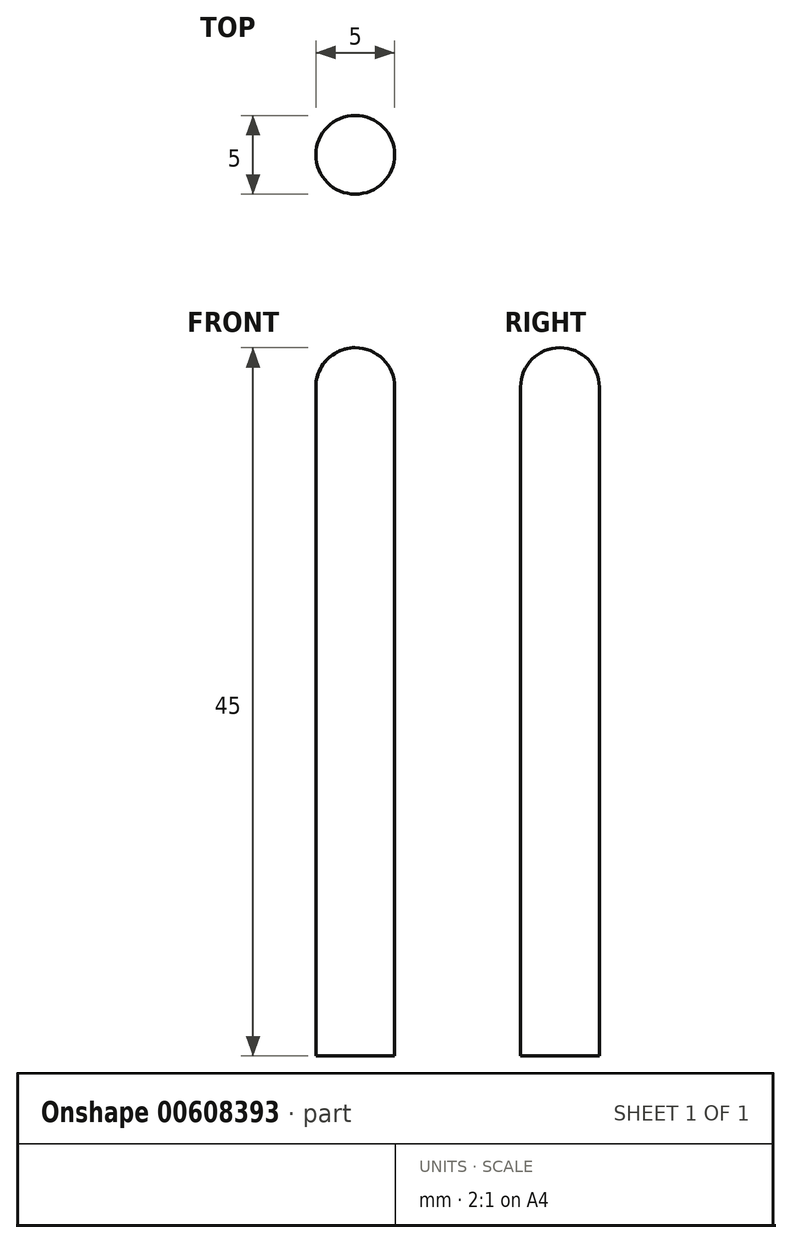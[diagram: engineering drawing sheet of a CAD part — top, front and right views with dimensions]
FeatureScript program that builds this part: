
annotation { "Feature Type Name" : "Feature", "Feature Type Description" : "" }
export const myFeature = defineFeature(function(context is Context, id is Id, definition is map)
    precondition{}
    {
        {
            var Q0;
            Q0=qCreatedBy(makeId("Front.planeOp"),FACE);
            var sketch = newSketch(context, id + "F0", { "sketchPlane" : qUnion([Q0])});
            skLineSegment(sketch, "E0", {"start": v(0, 45) * mm, "end": v(0, 0) * mm});
            skLineSegment(sketch, "E1", {"start": v(0, 0) * mm, "end": v(-2.5, 0) * mm});
            skLineSegment(sketch, "E2", {"start": v(-2.5, 0) * mm, "end": v(-2.5, 42.5) * mm});
            skArc(sketch, "E3", {"start": v(0, 45) * mm, "mid": v(-1.77, 44.27) * mm, "end": v(-2.5, 42.5) * mm});
            skSolve(sketch);
        }
        {
            var Q0;
            Q0=makeQuery(id+"F0.imprint","IMPRINT",FACE,{"disambiguationData":[TD([[makeQuery(id+"F0.imprint","IMPRINT",EDGE,{"derivedFrom":sQuery(id+"F0.wireOp",EDGE,"E0")}),-1.0]])]});
            var Q1;
            Q1=sQuery(id+"F0.wireOp",EDGE,"E0");
            revolve(context, id + "F1", {"surfaceOperationType" : NewSurfaceOperationType.NEW, "entities" : qUnion([Q0]), "axis" : qUnion([Q1]), "revolveType" : RevolveType.FULL});
        }
    });
